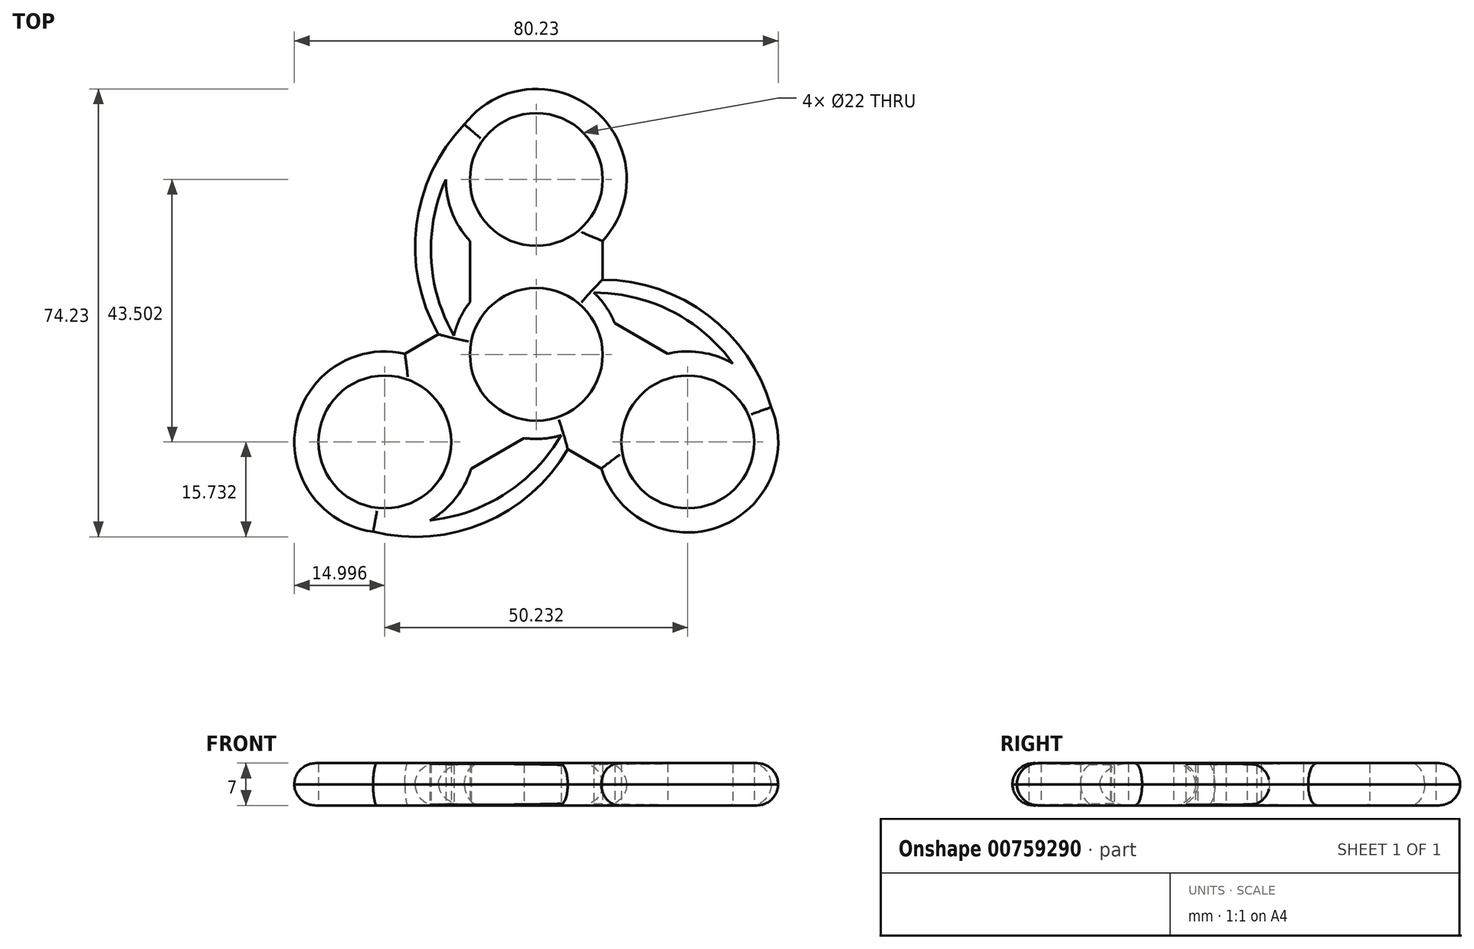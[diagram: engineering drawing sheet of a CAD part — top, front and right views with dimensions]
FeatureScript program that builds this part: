
annotation { "Feature Type Name" : "Feature", "Feature Type Description" : "" }
export const myFeature = defineFeature(function(context is Context, id is Id, definition is map)
    precondition{}
    {
        {
            var Q0;
            Q0=qCreatedBy(makeId("Top.planeOp"),FACE);
            var sketch = newSketch(context, id + "F0", { "sketchPlane" : qUnion([Q0])});
            skCircle(sketch, "E0", {"center": v(-47.97, 22.95) * mm, "radius": 14 * mm});
            skCircle(sketch, "E1", {"center": v(-47.97, 22.95) * mm, "radius": 11 * mm});
            skLineSegment(sketch, "E2", {"start": v(-47.97, 22.95) * mm, "end": v(-47.97, 66.95) * mm});
            skPoint(sketch, "E3", {"position": v(-47.97, 51.95) * mm});
            skCircle(sketch, "E4", {"center": v(-47.97, 51.95) * mm, "radius": 15 * mm});
            skCircle(sketch, "E5", {"center": v(-47.97, 51.95) * mm, "radius": 11 * mm});
            skLineSegment(sketch, "E6", {"start": v(-47.97, 51.95) * mm, "end": v(-36.97, 51.95) * mm});
            skLineSegment(sketch, "E7", {"start": v(-36.97, 51.95) * mm, "end": v(-58.97, 51.95) * mm});
            skLineSegment(sketch, "E8", {"start": v(-58.97, 41.76) * mm, "end": v(-58.97, 31.62) * mm});
            skLineSegment(sketch, "E9.MirrorCS", {"start": v(-36.97, 41.76) * mm, "end": v(-36.97, 31.62) * mm});
            skLineSegment(sketch, "E10", {"start": v(-47.97, 22.95) * mm, "end": v(-61.97, 22.95) * mm});
            skLineSegment(sketch, "E11", {"start": v(-61.97, 22.95) * mm, "end": v(-33.97, 22.95) * mm});
            skLineSegment(sketch, "E12", {"start": v(-58.97, 51.95) * mm, "end": v(-62.97, 51.95) * mm});
            skArc(sketch, "E13", {"start": v(-59.88, 61.07) * mm, "mid": v(-68.01, 42.4) * mm, "end": v(-61.97, 22.95) * mm});
            skArc(sketch, "E14", {"start": v(-62.97, 51.95) * mm, "mid": v(-65.4, 38.85) * mm, "end": v(-61.62, 26.07) * mm});
            skArc(sketch, "E15.1.0", {"start": v(-65.59, -4.54) * mm, "mid": v(-53.03, -0.09) * mm, "end": v(-43.85, 9.57) * mm});
            skArc(sketch, "E15.1.1", {"start": v(-75.02, -6.42) * mm, "mid": v(-54.79, -4.13) * mm, "end": v(-40.97, 10.83) * mm});
            skCircle(sketch, "E15.1.2", {"center": v(-73.08, 8.45) * mm, "radius": 11 * mm});
            skCircle(sketch, "E15.1.3", {"center": v(-73.08, 8.45) * mm, "radius": 15 * mm});
            skLineSegment(sketch, "E15.1.4", {"start": v(-58.75, 4.02) * mm, "end": v(-49.97, 9.1) * mm});
            skLineSegment(sketch, "E15.1.5", {"start": v(-69.75, 23.08) * mm, "end": v(-60.97, 28.15) * mm});
            skArc(sketch, "E15.2.0", {"start": v(-15.35, 21.44) * mm, "mid": v(-25.49, 30.1) * mm, "end": v(-38.44, 33.21) * mm});
            skArc(sketch, "E15.2.1", {"start": v(-9, 14.21) * mm, "mid": v(-21.1, 30.59) * mm, "end": v(-40.97, 35.08) * mm});
            skCircle(sketch, "E15.2.2", {"center": v(-22.85, 8.45) * mm, "radius": 11 * mm});
            skCircle(sketch, "E15.2.3", {"center": v(-22.85, 8.45) * mm, "radius": 15 * mm});
            skLineSegment(sketch, "E15.2.4", {"start": v(-26.18, 23.08) * mm, "end": v(-34.96, 28.15) * mm});
            skLineSegment(sketch, "E15.2.5", {"start": v(-37.18, 4.02) * mm, "end": v(-45.96, 9.1) * mm});
            skSolve(sketch);
        }
        {
            var Q0;
            {var subQ0=sQuery(id+"F0.wireOp",EDGE,"E12");Q0=makeQuery(id+"F0.imprint","IMPRINT",FACE,{"disambiguationData":[TD([[makeQuery(id+"F0.imprint","IMPRINT",EDGE,{"derivedFrom":subQ0}),1.0]])]});}
            var Q1;
            {var subQ0=sQuery(id+"F0.wireOp",EDGE,"E12");Q1=makeQuery(id+"F0.imprint","IMPRINT",FACE,{"disambiguationData":[TD([[makeQuery(id+"F0.imprint","IMPRINT",EDGE,{"derivedFrom":subQ0}),-1.0]])]});}
            var Q2;
            {var subQ0=sQuery(id+"F0.wireOp",EDGE,"E4");var subQ2=sQuery(id+"F0.wireOp",EDGE,"E2");var subQ3=makeQuery(id+"F0.imprint","INTERSECT",VERTEX,{"derivedFrom":[subQ2,subQ0]});Q2=makeQuery(id+"F0.imprint","IMPRINT",FACE,{"disambiguationData":[TD([[makeQuery(id+"F0.imprint","IMPRINT",EDGE,{"disambiguationData":[TD([[subQ3,1.0]])],"derivedFrom":subQ2}),-1.0]])]});}
            var Q3;
            {var subQ1=sQuery(id+"F0.wireOp",EDGE,"E4");var subQ3=sQuery(id+"F0.wireOp",EDGE,"E13");var subQ4=makeQuery(id+"F0.imprint","INTERSECT",VERTEX,{"derivedFrom":[subQ1,subQ3]});Q3=makeQuery(id+"F0.imprint","IMPRINT",FACE,{"disambiguationData":[TD([[makeQuery(id+"F0.imprint","IMPRINT",EDGE,{"disambiguationData":[TD([[subQ4,-1.0]])],"derivedFrom":subQ3}),1.0]])]});}
            var Q4;
            {var subQ3=sQuery(id+"F0.wireOp",EDGE,"E8");Q4=makeQuery(id+"F0.imprint","IMPRINT",FACE,{"disambiguationData":[TD([[makeQuery(id+"F0.imprint","IMPRINT",EDGE,{"derivedFrom":subQ3}),1.0]])]});}
            var Q5;
            {var subQ0=sQuery(id+"F0.wireOp",EDGE,"E4");var subQ5=sQuery(id+"F0.wireOp",EDGE,"E9.MirrorCS");var subQ6=makeQuery(id+"F0.imprint","INTERSECT",VERTEX,{"derivedFrom":[subQ0,subQ5]});Q5=makeQuery(id+"F0.imprint","IMPRINT",FACE,{"disambiguationData":[TD([[makeQuery(id+"F0.imprint","IMPRINT",EDGE,{"disambiguationData":[TD([[subQ6,-1.0]])],"derivedFrom":subQ5}),-1.0]])]});}
            var Q6;
            {var subQ0=sQuery(id+"F0.wireOp",EDGE,"E15.2.0");var subQ1=sQuery(id+"F0.wireOp",EDGE,"E0");var subQ2=makeQuery(id+"F0.imprint","INTERSECT",VERTEX,{"derivedFrom":[subQ1,subQ0]});Q6=makeQuery(id+"F0.imprint","IMPRINT",FACE,{"disambiguationData":[TD([[makeQuery(id+"F0.imprint","IMPRINT",EDGE,{"disambiguationData":[TD([[subQ2,-1.0]])],"derivedFrom":subQ1}),-1.0]])]});}
            var Q7;
            {var subQ0=sQuery(id+"F0.wireOp",EDGE,"E15.2.1");var subQ1=sQuery(id+"F0.wireOp",EDGE,"E9.MirrorCS");var subQ2=makeQuery(id+"F0.imprint","INTERSECT",VERTEX,{"derivedFrom":[subQ1,subQ0]});Q7=makeQuery(id+"F0.imprint","IMPRINT",FACE,{"disambiguationData":[TD([[makeQuery(id+"F0.imprint","IMPRINT",EDGE,{"disambiguationData":[TD([[subQ2,-1.0]])],"derivedFrom":subQ1}),1.0]])]});}
            var Q8;
            {var subQ2=sQuery(id+"F0.wireOp",EDGE,"E15.2.4");Q8=makeQuery(id+"F0.imprint","IMPRINT",FACE,{"disambiguationData":[TD([[makeQuery(id+"F0.imprint","IMPRINT",EDGE,{"derivedFrom":subQ2}),1.0]])]});}
            var Q9;
            {var subQ0=sQuery(id+"F0.wireOp",EDGE,"E15.1.1");var subQ1=sQuery(id+"F0.wireOp",EDGE,"E0");var subQ2=makeQuery(id+"F0.imprint","INTERSECT",VERTEX,{"derivedFrom":[subQ1,subQ0]});Q9=makeQuery(id+"F0.imprint","IMPRINT",FACE,{"disambiguationData":[TD([[makeQuery(id+"F0.imprint","IMPRINT",EDGE,{"disambiguationData":[TD([[subQ2,-1.0]])],"derivedFrom":subQ1}),-1.0]])]});}
            var Q10;
            Q10=makeQuery(id+"F0.imprint","IMPRINT",FACE,{"disambiguationData":[TD([[makeQuery(id+"F0.imprint","IMPRINT",EDGE,{"derivedFrom":sQuery(id+"F0.wireOp",EDGE,"E15.2.2")}),-1.0]])]});
            var Q11;
            {var subQ0=sQuery(id+"F0.wireOp",EDGE,"E0");var subQ9=sQuery(id+"F0.wireOp",EDGE,"E11");var subQ10=makeQuery(id+"F0.imprint","INTERSECT",VERTEX,{"derivedFrom":[subQ0,subQ9]});Q11=makeQuery(id+"F0.imprint","IMPRINT",FACE,{"disambiguationData":[TD([[makeQuery(id+"F0.imprint","IMPRINT",EDGE,{"disambiguationData":[TD([[subQ10,-1.0]])],"derivedFrom":subQ0}),1.0]])]});}
            var Q12;
            {var subQ1=sQuery(id+"F0.wireOp",EDGE,"E0");var subQ5=makeQuery(id+"F0.imprint","INTERSECT",VERTEX,{"derivedFrom":[subQ1,sQuery(id+"F0.wireOp",EDGE,"E8")]});Q12=makeQuery(id+"F0.imprint","IMPRINT",FACE,{"disambiguationData":[TD([[makeQuery(id+"F0.imprint","IMPRINT",EDGE,{"disambiguationData":[TD([[subQ5,-1.0]])],"derivedFrom":subQ1}),1.0]])]});}
            var Q13;
            {var subQ0=sQuery(id+"F0.wireOp",EDGE,"E0");var subQ3=makeQuery(id+"F0.imprint","INTERSECT",VERTEX,{"derivedFrom":[subQ0,sQuery(id+"F0.wireOp",EDGE,"E15.1.4")]});Q13=makeQuery(id+"F0.imprint","IMPRINT",FACE,{"disambiguationData":[TD([[makeQuery(id+"F0.imprint","IMPRINT",EDGE,{"disambiguationData":[TD([[subQ3,1.0]])],"derivedFrom":subQ0}),1.0]])]});}
            var Q14;
            {var subQ0=sQuery(id+"F0.wireOp",EDGE,"E15.1.3");var subQ1=sQuery(id+"F0.wireOp",EDGE,"E15.1.0");var subQ2=makeQuery(id+"F0.imprint","INTERSECT",VERTEX,{"derivedFrom":[subQ1,subQ0]});Q14=makeQuery(id+"F0.imprint","IMPRINT",FACE,{"disambiguationData":[TD([[makeQuery(id+"F0.imprint","IMPRINT",EDGE,{"disambiguationData":[TD([[subQ2,-1.0]])],"derivedFrom":subQ1}),-1.0]])]});}
            var Q15;
            Q15=makeQuery(id+"F0.imprint","IMPRINT",FACE,{"disambiguationData":[TD([[makeQuery(id+"F0.imprint","IMPRINT",EDGE,{"derivedFrom":sQuery(id+"F0.wireOp",EDGE,"E15.1.2")}),-1.0]])]});
            var Q16;
            {var subQ1=sQuery(id+"F0.wireOp",EDGE,"E0");var subQ3=sQuery(id+"F0.wireOp",EDGE,"E14");var subQ4=makeQuery(id+"F0.imprint","INTERSECT",VERTEX,{"derivedFrom":[subQ1,subQ3]});Q16=makeQuery(id+"F0.imprint","IMPRINT",FACE,{"disambiguationData":[TD([[makeQuery(id+"F0.imprint","IMPRINT",EDGE,{"disambiguationData":[TD([[subQ4,1.0]])],"derivedFrom":subQ3}),-1.0]])]});}
            var Q17;
            {var subQ3=sQuery(id+"F0.wireOp",EDGE,"E15.1.3");var subQ5=sQuery(id+"F0.wireOp",EDGE,"E15.1.5");var subQ7=makeQuery(id+"F0.imprint","INTERSECT",VERTEX,{"derivedFrom":[subQ3,subQ5]});Q17=makeQuery(id+"F0.imprint","IMPRINT",FACE,{"disambiguationData":[TD([[makeQuery(id+"F0.imprint","IMPRINT",EDGE,{"disambiguationData":[TD([[subQ7,1.0]])],"derivedFrom":subQ3}),-1.0]])]});}
            var Q18;
            {var subQ0=sQuery(id+"F0.wireOp",EDGE,"E15.1.4");Q18=makeQuery(id+"F0.imprint","IMPRINT",FACE,{"disambiguationData":[TD([[makeQuery(id+"F0.imprint","IMPRINT",EDGE,{"derivedFrom":subQ0}),1.0]])]});}
            var Q19;
            {var subQ0=sQuery(id+"F0.wireOp",EDGE,"E15.1.0");var subQ1=sQuery(id+"F0.wireOp",EDGE,"E0");var subQ2=makeQuery(id+"F0.imprint","INTERSECT",VERTEX,{"derivedFrom":[subQ1,subQ0]});Q19=makeQuery(id+"F0.imprint","IMPRINT",FACE,{"disambiguationData":[TD([[makeQuery(id+"F0.imprint","IMPRINT",EDGE,{"disambiguationData":[TD([[subQ2,-1.0]])],"derivedFrom":subQ1}),-1.0]])]});}
            extrude(context, id + "F1", {"entities" : qUnion([Q0, Q1, Q2, Q3, Q4, Q5, Q6, Q7, Q8, Q9, Q10, Q11, Q12, Q13, Q14, Q15, Q16, Q17, Q18, Q19]), "depth" : 7 * mm, "offsetDistance" : 25.4 * mm});
        }
        {
            var Q0;
            Q0=makeQuery(id+"F1.opExtrude","CAP_EDGE",EDGE,{"disambiguationData":[OSD([sQuery(id+"F0.wireOp",EDGE,"E13")])],"isStart":false});
            var Q1;
            {var subQ0=sQuery(id+"F0.wireOp",EDGE,"E4");Q1=makeQuery(id+"F1.opExtrude","CAP_EDGE",EDGE,{"disambiguationData":[OSD([subQ0]),TDD([makeQuery(id+"F0.imprint","IMPRINT",EDGE,{"disambiguationData":[TD([[makeQuery(id+"F0.imprint","INTERSECT",VERTEX,{"derivedFrom":[subQ0,sQuery(id+"F0.wireOp",EDGE,"E13")]}),1.0]])],"derivedFrom":subQ0}),makeQuery(id+"F0.imprint","IMPRINT",EDGE,{"disambiguationData":[TD([[makeQuery(id+"F0.imprint","INTERSECT",VERTEX,{"derivedFrom":[subQ0,sQuery(id+"F0.wireOp",EDGE,"E9.MirrorCS")]}),-1.0]])],"derivedFrom":subQ0})])],"isStart":false});}
            var Q2;
            Q2=makeQuery(id+"F1.opExtrude","CAP_EDGE",EDGE,{"disambiguationData":[OSD([sQuery(id+"F0.wireOp",EDGE,"E15.2.1")])],"isStart":false});
            var Q3;
            {var subQ0=sQuery(id+"F0.wireOp",EDGE,"E15.2.3");Q3=makeQuery(id+"F1.opExtrude","CAP_EDGE",EDGE,{"disambiguationData":[OSD([subQ0]),TDD([makeQuery(id+"F0.imprint","IMPRINT",EDGE,{"disambiguationData":[TD([[makeQuery(id+"F0.imprint","INTERSECT",VERTEX,{"derivedFrom":[sQuery(id+"F0.wireOp",EDGE,"E15.2.1"),subQ0]}),1.0]])],"derivedFrom":subQ0})])],"isStart":false});}
            var Q4;
            Q4=makeQuery(id+"F1.opExtrude","CAP_EDGE",EDGE,{"disambiguationData":[OSD([sQuery(id+"F0.wireOp",EDGE,"E15.2.5")])],"isStart":false});
            var Q5;
            Q5=makeQuery(id+"F1.opExtrude","CAP_EDGE",EDGE,{"disambiguationData":[OSD([sQuery(id+"F0.wireOp",EDGE,"E15.1.1")])],"isStart":false});
            var Q6;
            {var subQ0=sQuery(id+"F0.wireOp",EDGE,"E15.1.3");Q6=makeQuery(id+"F1.opExtrude","CAP_EDGE",EDGE,{"disambiguationData":[OSD([subQ0]),TDD([makeQuery(id+"F0.imprint","IMPRINT",EDGE,{"disambiguationData":[TD([[makeQuery(id+"F0.imprint","INTERSECT",VERTEX,{"derivedFrom":[sQuery(id+"F0.wireOp",EDGE,"E15.1.1"),subQ0]}),1.0]])],"derivedFrom":subQ0})])],"isStart":false});}
            var Q7;
            Q7=makeQuery(id+"F1.opExtrude","CAP_EDGE",EDGE,{"disambiguationData":[OSD([sQuery(id+"F0.wireOp",EDGE,"E15.1.5")])],"isStart":false});
            var Q8;
            Q8=makeQuery(id+"F1.opExtrude","CAP_EDGE",EDGE,{"disambiguationData":[OSD([sQuery(id+"F0.wireOp",EDGE,"E9.MirrorCS")])],"isStart":false});
            fillet(context, id + "F2", {"entities" : qUnion([Q0, Q1, Q2, Q3, Q4, Q5, Q6, Q7, Q8]), "radius" : 3.52 * mm, "tangentPropagation" : true, "allowEdgeOverflow" : false});
        }
        {
            var Q0;
            {var subQ0=sQuery(id+"F0.wireOp",EDGE,"E15.1.3");Q0=makeQuery(id+"F1.opExtrude","CAP_EDGE",EDGE,{"disambiguationData":[OSD([subQ0]),TDD([makeQuery(id+"F0.imprint","IMPRINT",EDGE,{"disambiguationData":[TD([[makeQuery(id+"F0.imprint","INTERSECT",VERTEX,{"derivedFrom":[sQuery(id+"F0.wireOp",EDGE,"E15.1.1"),subQ0]}),1.0]])],"derivedFrom":subQ0})])],"isStart":true});}
            var Q1;
            Q1=makeQuery(id+"F1.opExtrude","CAP_EDGE",EDGE,{"disambiguationData":[OSD([sQuery(id+"F0.wireOp",EDGE,"E15.1.1")])],"isStart":true});
            var Q2;
            Q2=makeQuery(id+"F1.opExtrude","CAP_EDGE",EDGE,{"disambiguationData":[OSD([sQuery(id+"F0.wireOp",EDGE,"E15.1.5")])],"isStart":true});
            var Q3;
            Q3=makeQuery(id+"F1.opExtrude","CAP_EDGE",EDGE,{"disambiguationData":[OSD([sQuery(id+"F0.wireOp",EDGE,"E13")])],"isStart":true});
            var Q4;
            {var subQ0=sQuery(id+"F0.wireOp",EDGE,"E4");Q4=makeQuery(id+"F1.opExtrude","CAP_EDGE",EDGE,{"disambiguationData":[OSD([subQ0]),TDD([makeQuery(id+"F0.imprint","IMPRINT",EDGE,{"disambiguationData":[TD([[makeQuery(id+"F0.imprint","INTERSECT",VERTEX,{"derivedFrom":[subQ0,sQuery(id+"F0.wireOp",EDGE,"E13")]}),1.0]])],"derivedFrom":subQ0}),makeQuery(id+"F0.imprint","IMPRINT",EDGE,{"disambiguationData":[TD([[makeQuery(id+"F0.imprint","INTERSECT",VERTEX,{"derivedFrom":[subQ0,sQuery(id+"F0.wireOp",EDGE,"E9.MirrorCS")]}),-1.0]])],"derivedFrom":subQ0})])],"isStart":true});}
            var Q5;
            Q5=makeQuery(id+"F1.opExtrude","CAP_EDGE",EDGE,{"disambiguationData":[OSD([sQuery(id+"F0.wireOp",EDGE,"E9.MirrorCS")])],"isStart":true});
            var Q6;
            Q6=makeQuery(id+"F1.opExtrude","CAP_EDGE",EDGE,{"disambiguationData":[OSD([sQuery(id+"F0.wireOp",EDGE,"E15.2.1")])],"isStart":true});
            var Q7;
            {var subQ0=sQuery(id+"F0.wireOp",EDGE,"E15.2.3");Q7=makeQuery(id+"F1.opExtrude","CAP_EDGE",EDGE,{"disambiguationData":[OSD([subQ0]),TDD([makeQuery(id+"F0.imprint","IMPRINT",EDGE,{"disambiguationData":[TD([[makeQuery(id+"F0.imprint","INTERSECT",VERTEX,{"derivedFrom":[sQuery(id+"F0.wireOp",EDGE,"E15.2.1"),subQ0]}),1.0]])],"derivedFrom":subQ0})])],"isStart":true});}
            var Q8;
            Q8=makeQuery(id+"F1.opExtrude","CAP_EDGE",EDGE,{"disambiguationData":[OSD([sQuery(id+"F0.wireOp",EDGE,"E15.2.5")])],"isStart":true});
            fillet(context, id + "F3", {"entities" : qUnion([Q0, Q1, Q2, Q3, Q4, Q5, Q6, Q7, Q8]), "radius" : 3.52 * mm, "tangentPropagation" : true, "allowEdgeOverflow" : false});
        }
    });
